# Revit family: BasinMixer-CountertopPhotocellMixer-WithMains-Vitra-AquaSeeSeries-A47060
name_source: partatom
category: Plumbing Fixtures
revit_build: Autodesk Revit 2017 (Build: 20160225_1515(x64)
units: mm (PartAtom-declared; Revit-internal decimal feet)

## family parameters
Cut with Voids When Loaded = No
Host = Face
OmniClass Number = 23.45.55.17
OmniClass Title = Mixing Faucets
Part Type = Normal
Room Calculation Point = No
Round Connector Dimension = Use Diameter
Shared = Yes

## types (1)
- BasinMixer-CountertopPhotocellMixer-WithMains-Vitra-AquaSeeSeries-A47060
    Article No. (default) = A47060
    BIMobject category = Taps & Mixers
    Brand = VitrA
    CW Connection = Yes
    Coating Material = Chrome (Metal)
    Color = Chrome
    Connection Diameter (mm) = 10 mm  [stored 0.0328084 ft]
    Default Elevation = 850 mm
    Description = Touch Free Basin Mixer - Counter top (Mains) Hot-Cold Water Inlet
    Design country = Turkey
    Flow Rate(L/min. - 3 bar) = 5 L/min.
    HW Connection = Yes
    Hot Water Supply (max.) = 80 °C
    Hot Water temperature, factory set to = 38 °C
    IFC Classification = Sanitary Terminal
    Main Material = Brass
    Manufacturer = Vitra
    Manufacturer name = Vitra
    Masterformat 2014 Code = 22 40 00
    Masterformat 2014 Description = Plumbing Fixtures
    Min. flow pressure of = 0.5 bar
    Model = A47060
    Mounting type = Countertop
    NBS Referans Code = 45-35-70/371
    NBS Referans Description = Water supply fittings for wash basins and troughs
    Nominal Depth (mm) = 170 mm  [stored 0.557743 ft]
    Nominal Height (mm) = 120 mm  [stored 0.393701 ft]
    Nominal Width (mm) = 70 mm
    Number Of Connections = 2
    OmniClass Code = 23.45.55.17
    OmniClass Description = Mixing Faucets
    Power Source Battery = No
    Power Source Mains = Yes
    Product Properties = Energy Saving
    Product SKU = A47060
    Product Type = Basin Mixer
    Product certification = https://www.vitraglobal.com
    Product family = AquaSee
    Product group = AquaSee Basin Mixer
    Product url = https://www.vitra.com.tr
    Range of Hot Water Supply = 5 - 65 °C
    Range of flow pressure = 1 - 5 bar
    Technical description = https://www.vitra.com.tr
    Test Pressure = 16 bar
    URL = https://vitraglobal.com
    Uniclass 1.4 Code = L725111
    Uniclass 1.4 Description = Mixer taps
    Uniclass 2.0 Code = Pr_40_30_96_98
    Uniclass 2.0 Description = Washbasin Tap
    Uniclass 2015 Code = Pr_40_20_87_98
    Uniclass 2015 Name = Washbasin Tap
    Uniformat II Code = 22 40 00
    Uniformat II Description = Plumbing Fixture
    Vent Connection = No
    Warranty Period (Year) = 2 Years
    Waste Connection = No
    Weight Net (kg) = 2.57
    Youtube = https://www.youtube.com

note: [stored X ft] marks values corroborated as IEEE doubles in the binary element streams (Revit-internal decimal feet)

## geometry (parser evidence)
native form markers: Sweep x2
no freeform markers — native parametric forms only
